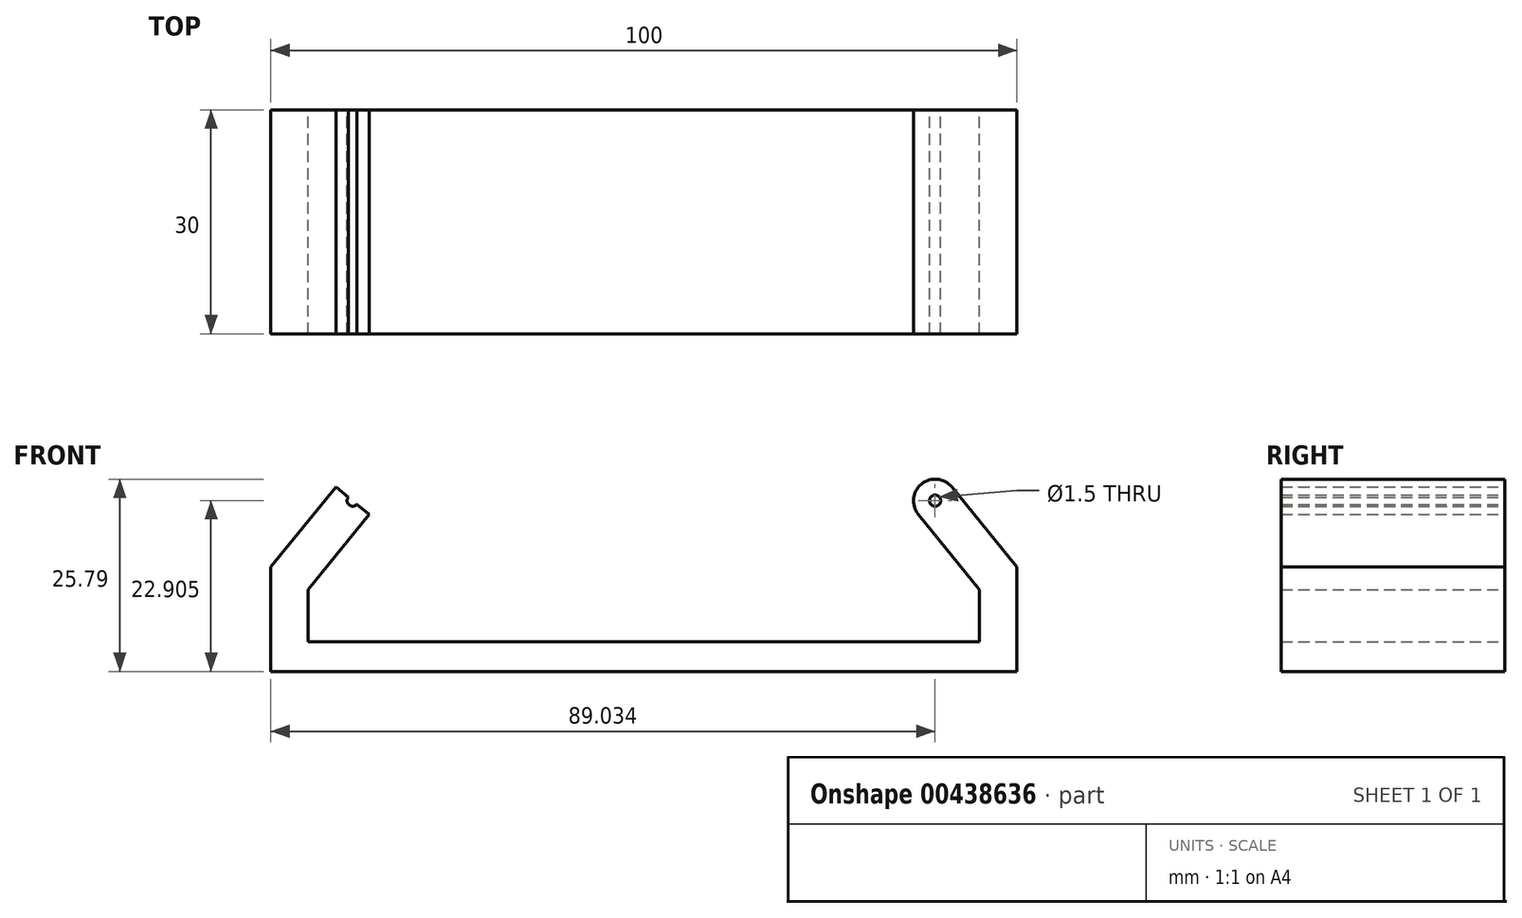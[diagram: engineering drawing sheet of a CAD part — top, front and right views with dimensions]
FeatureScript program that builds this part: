
annotation { "Feature Type Name" : "Feature", "Feature Type Description" : "" }
export const myFeature = defineFeature(function(context is Context, id is Id, definition is map)
    precondition{}
    {
        {
            var Q0;
            Q0=qCreatedBy(makeId("Front.planeOp"),FACE);
            var sketch = newSketch(context, id + "F0", { "sketchPlane" : qUnion([Q0])});
            skCircle(sketch, "E0", {"center": v(0, 39.93) * mm, "radius": 20 * mm});
            skLineSegment(sketch, "E1.bottom", {"start": v(50, 2) * mm, "end": v(-50, 2) * mm});
            skLineSegment(sketch, "E1.top", {"start": v(50, -2) * mm, "end": v(-50, -2) * mm});
            skLineSegment(sketch, "E1.left", {"start": v(50, 2) * mm, "end": v(50, -2) * mm});
            skLineSegment(sketch, "E1.right", {"start": v(-50, 2) * mm, "end": v(-50, -2) * mm});
            skPoint(sketch, "E1.middle", {"position": v(0, 0) * mm});
            skLineSegment(sketch, "E2", {"start": v(-50, 2) * mm, "end": v(-50, 12) * mm});
            skLineSegment(sketch, "E3", {"start": v(-45, 9) * mm, "end": v(-45, 2) * mm});
            skLineSegment(sketch, "E4", {"start": v(-45, 9) * mm, "end": v(-36.8, 19.08) * mm});
            skLineSegment(sketch, "E5", {"start": v(-50, 12) * mm, "end": v(-41.27, 22.73) * mm});
            skLineSegment(sketch, "E6", {"start": v(-36.8, 19.08) * mm, "end": v(-41.27, 22.73) * mm});
            skArc(sketch, "E7", {"start": v(-41.27, 22.73) * mm, "mid": v(-37.21, 23.14) * mm, "end": v(-36.8, 19.08) * mm});
            skCircle(sketch, "E8", {"center": v(-39.03, 20.9) * mm, "radius": 0.75 * mm});
            skCircle(sketch, "E9.MirrorC", {"center": v(39.03, 20.9) * mm, "radius": 0.75 * mm});
            skLineSegment(sketch, "E10.MirrorCS", {"start": v(45, 9) * mm, "end": v(45, 2) * mm});
            skLineSegment(sketch, "E11.MirrorCS", {"start": v(50, 2) * mm, "end": v(50, 12) * mm});
            skLineSegment(sketch, "E12.MirrorCS", {"start": v(45, 9) * mm, "end": v(36.8, 19.08) * mm});
            skArc(sketch, "E13.MirrorCS", {"start": v(41.27, 22.73) * mm, "mid": v(37.21, 23.14) * mm, "end": v(36.8, 19.08) * mm});
            skLineSegment(sketch, "E14.MirrorCS", {"start": v(36.8, 19.08) * mm, "end": v(41.27, 22.73) * mm});
            skLineSegment(sketch, "E15.MirrorCS", {"start": v(50, 12) * mm, "end": v(41.27, 22.73) * mm});
            skSolve(sketch);
        }
        {
            var Q0;
            {var subQ0=sQuery(id+"F0.wireOp",EDGE,"E7");Q0=makeQuery(id+"F0.imprint","IMPRINT",FACE,{"disambiguationData":[TD([[makeQuery(id+"F0.imprint","IMPRINT",EDGE,{"derivedFrom":subQ0}),-1.0]])]});}
            var Q1;
            {var subQ1=sQuery(id+"F0.wireOp",EDGE,"E2");Q1=makeQuery(id+"F0.imprint","IMPRINT",FACE,{"disambiguationData":[TD([[makeQuery(id+"F0.imprint","IMPRINT",EDGE,{"derivedFrom":subQ1}),-1.0]])]});}
            var Q2;
            Q2=makeQuery(id+"F0.imprint","IMPRINT",FACE,{"disambiguationData":[TD([[makeQuery(id+"F0.imprint","IMPRINT",EDGE,{"derivedFrom":sQuery(id+"F0.wireOp",EDGE,"E1.top")}),-1.0]])]});
            var Q3;
            {var subQ1=sQuery(id+"F0.wireOp",EDGE,"E10.MirrorCS");Q3=makeQuery(id+"F0.imprint","IMPRINT",FACE,{"disambiguationData":[TD([[makeQuery(id+"F0.imprint","IMPRINT",EDGE,{"derivedFrom":subQ1}),1.0]])]});}
            var Q4;
            {var subQ4=sQuery(id+"F0.wireOp",EDGE,"E13.MirrorCS");Q4=makeQuery(id+"F0.imprint","IMPRINT",FACE,{"disambiguationData":[TD([[makeQuery(id+"F0.imprint","IMPRINT",EDGE,{"derivedFrom":subQ4}),1.0]])]});}
            extrude(context, id + "F1", {"entities" : qUnion([Q0, Q1, Q2, Q3, Q4]), "endBound" : BoundingType.SYMMETRIC, "depth" : 30 * mm});
        }
    });
